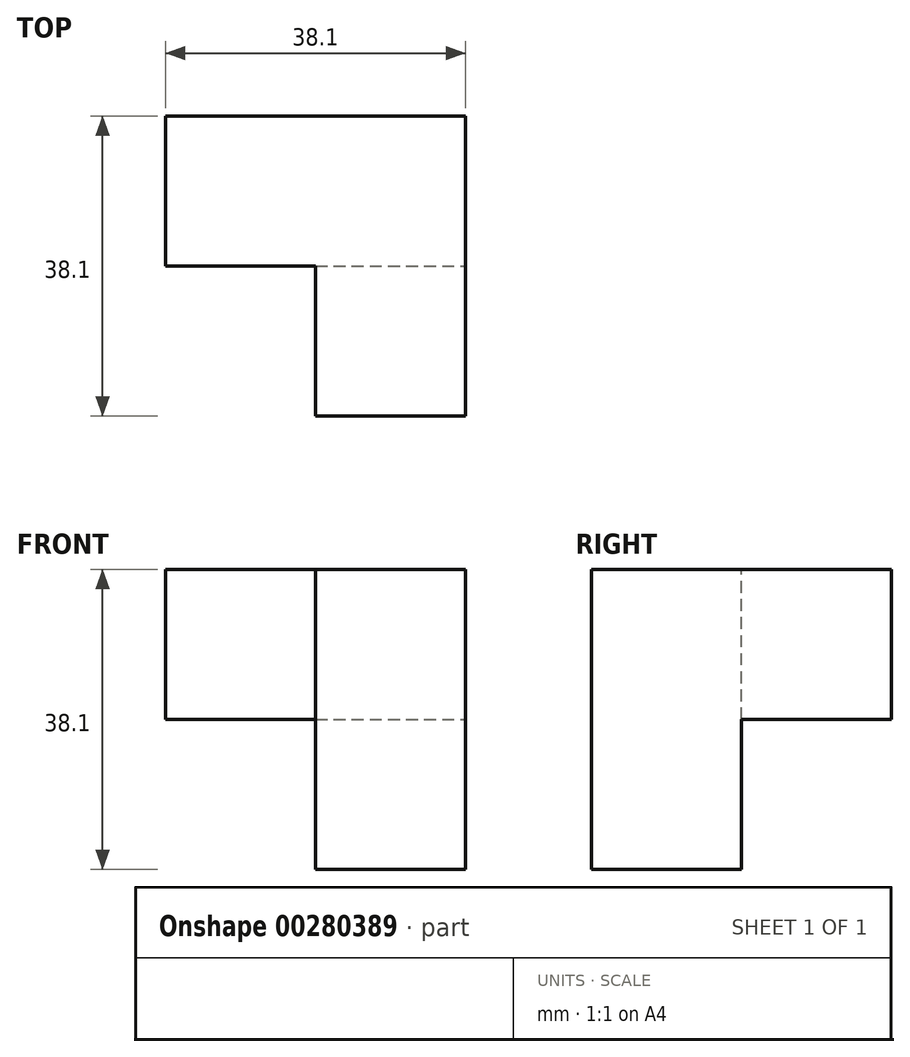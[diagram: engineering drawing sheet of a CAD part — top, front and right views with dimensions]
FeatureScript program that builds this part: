
annotation { "Feature Type Name" : "Feature", "Feature Type Description" : "" }
export const myFeature = defineFeature(function(context is Context, id is Id, definition is map)
    precondition{}
    {
        {
            var Q0;
            Q0=qCreatedBy(makeId("Top.planeOp"),FACE);
            var sketch = newSketch(context, id + "F0", { "sketchPlane" : qUnion([Q0])});
            skLineSegment(sketch, "E0.bottom", {"start": v(0, 0) * mm, "end": v(19.05, 0) * mm});
            skLineSegment(sketch, "E0.top", {"start": v(0, 38.1) * mm, "end": v(19.05, 38.1) * mm});
            skLineSegment(sketch, "E0.left", {"start": v(0, 0) * mm, "end": v(0, 38.1) * mm});
            skLineSegment(sketch, "E0.right", {"start": v(19.05, 0) * mm, "end": v(19.05, 38.1) * mm});
            skSolve(sketch);
        }
        {
            var Q0;
            Q0 = qSketchRegion(id + "F0", true);
            extrude(context, id + "F1", {"entities" : qUnion([Q0]), "depth" : 19.05 * mm});
        }
        {
            var Q0;
            Q0=makeQuery(id+"F1.opExtrude","SWEPT_FACE",FACE,{"disambiguationData":[OSD([sQuery(id+"F0.wireOp",EDGE,"E0.left")])]});
            var sketch = newSketch(context, id + "F2", { "sketchPlane" : qUnion([Q0])});
            skLineSegment(sketch, "E1.bottom", {"start": v(-38.1, 0) * mm, "end": v(-19.05, 0) * mm});
            skLineSegment(sketch, "E1.top", {"start": v(-38.1, 19.05) * mm, "end": v(-19.05, 19.05) * mm});
            skLineSegment(sketch, "E1.left", {"start": v(-38.1, 0) * mm, "end": v(-38.1, 19.05) * mm});
            skLineSegment(sketch, "E1.right", {"start": v(-19.05, 0) * mm, "end": v(-19.05, 19.05) * mm});
            skSolve(sketch);
        }
        {
            var Q0;
            Q0 = qSketchRegion(id + "F2", true);
            extrude(context, id + "F3", {"entities" : qUnion([Q0]), "operationType" : NewBodyOperationType.ADD, "depth" : 19.05 * mm});
        }
        {
            var Q0;
            Q0=makeQuery(id+"F3.boolean.opBoolean","MERGE",FACE,{"derivedFrom":[makeQuery(id+"F1.opExtrude","CAP_FACE",FACE,{"disambiguationData":[OSD([sQuery(id+"F0.wireOp",EDGE,"E0.bottom"),sQuery(id+"F0.wireOp",EDGE,"E0.top"),sQuery(id+"F0.wireOp",EDGE,"E0.left"),sQuery(id+"F0.wireOp",EDGE,"E0.right")])],"isStart":true}),makeQuery(id+"F3.opExtrude","SWEPT_FACE",FACE,{"disambiguationData":[OSD([sQuery(id+"F2.wireOp",EDGE,"E1.bottom")])]})]});
            var sketch = newSketch(context, id + "F4", { "sketchPlane" : qUnion([Q0])});
            skLineSegment(sketch, "E2.bottom", {"start": v(0, 0) * mm, "end": v(19.05, 0) * mm});
            skLineSegment(sketch, "E2.top", {"start": v(0, -19.05) * mm, "end": v(19.05, -19.05) * mm});
            skLineSegment(sketch, "E2.left", {"start": v(0, 0) * mm, "end": v(0, -19.05) * mm});
            skLineSegment(sketch, "E2.right", {"start": v(19.05, 0) * mm, "end": v(19.05, -19.05) * mm});
            skSolve(sketch);
        }
        {
            var Q0;
            Q0 = qSketchRegion(id + "F4", true);
            extrude(context, id + "F5", {"entities" : qUnion([Q0]), "operationType" : NewBodyOperationType.ADD, "depth" : 19.05 * mm});
        }
    });
